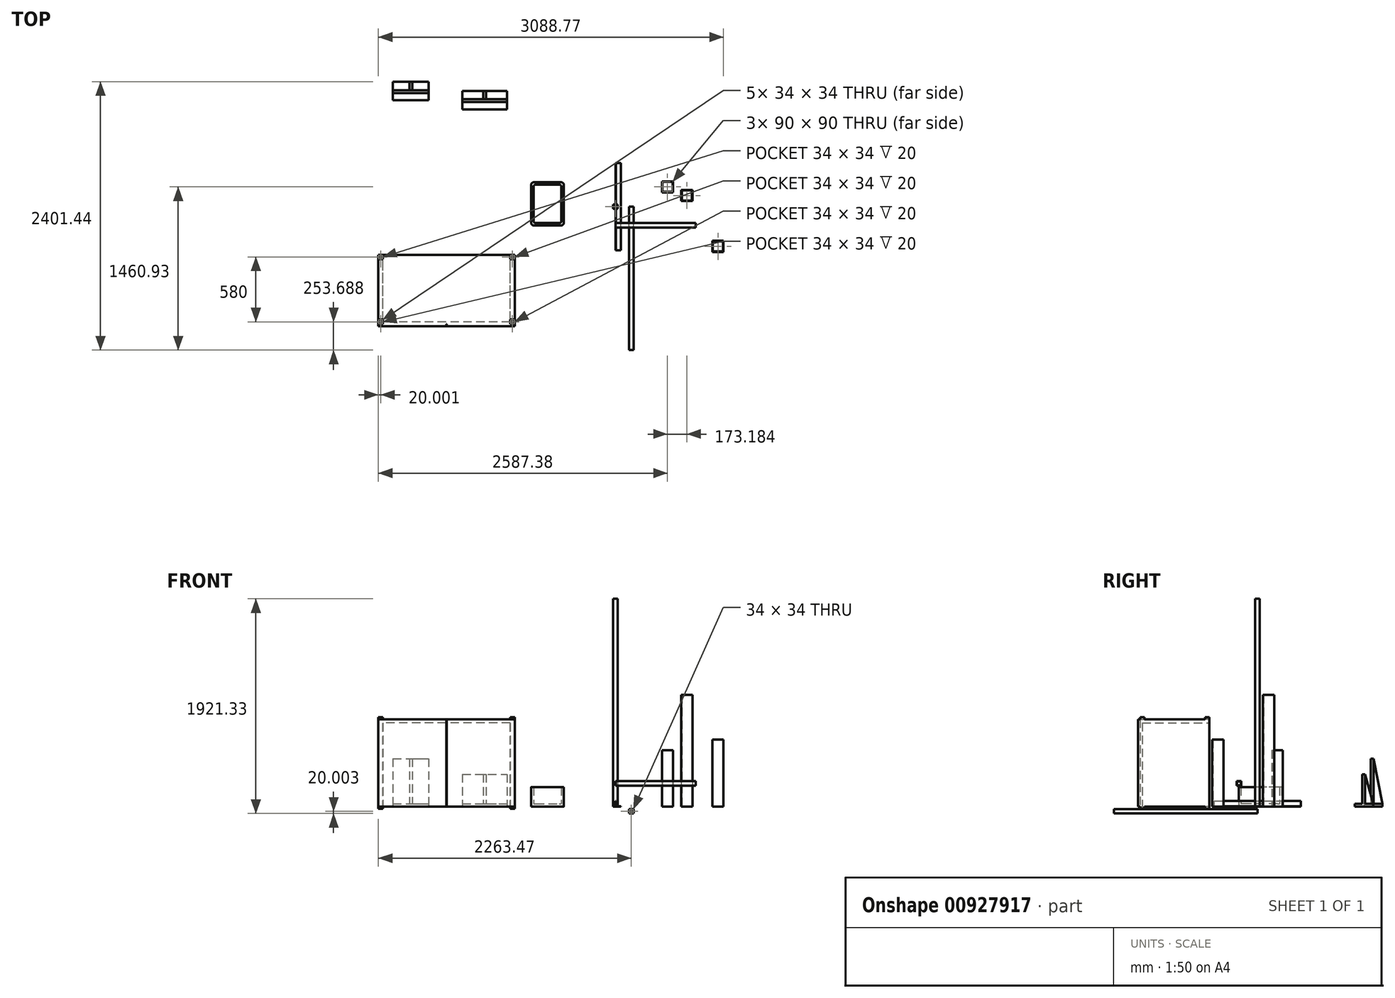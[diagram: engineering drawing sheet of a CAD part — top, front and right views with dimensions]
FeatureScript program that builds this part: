
annotation { "Feature Type Name" : "Feature", "Feature Type Description" : "" }
export const myFeature = defineFeature(function(context is Context, id is Id, definition is map)
    precondition{}
    {
        {
            var Q0;
            Q0=qCreatedBy(makeId("Front.planeOp"),FACE);
            var sketch = newSketch(context, id + "F0", { "sketchPlane" : qUnion([Q0])});
            skLineSegment(sketch, "E0", {"start": v(0, 0) * mm, "end": v(50, 0) * mm});
            skLineSegment(sketch, "E1", {"start": v(0, 0) * mm, "end": v(0, 50) * mm});
            skLineSegment(sketch, "E2", {"start": v(50, 3) * mm, "end": v(3, 3) * mm});
            skLineSegment(sketch, "E3", {"start": v(3, 50) * mm, "end": v(3, 3) * mm});
            skLineSegment(sketch, "E4", {"start": v(0, 50) * mm, "end": v(3, 50) * mm});
            skLineSegment(sketch, "E5", {"start": v(50, 0) * mm, "end": v(50, 3) * mm});
            skSolve(sketch);
        }
        {
            var Q0;
            Q0=makeQuery(id+"F0.imprint","IMPRINT",FACE,{"disambiguationData":[TD([[makeQuery(id+"F0.imprint","IMPRINT",EDGE,{"derivedFrom":sQuery(id+"F0.wireOp",EDGE,"E0")}),1.0]])]});
            extrude(context, id + "F1", {"entities" : qUnion([Q0]), "depth" : 780 * mm, "offsetDistance" : 25 * mm, "symmetric" : true});
        }
        {
            var Q0;
            Q0=qCreatedBy(makeId("Top.planeOp"),FACE);
            var sketch = newSketch(context, id + "F2", { "sketchPlane" : qUnion([Q0])});
            skLineSegment(sketch, "E6.bottom", {"start": v(-20, 20) * mm, "end": v(20, 20) * mm});
            skLineSegment(sketch, "E6.top", {"start": v(-20, -20) * mm, "end": v(20, -20) * mm});
            skLineSegment(sketch, "E6.left", {"start": v(-20, 20) * mm, "end": v(-20, -20) * mm});
            skLineSegment(sketch, "E6.right", {"start": v(20, 20) * mm, "end": v(20, -20) * mm});
            skLineSegment(sketch, "E7.0", {"start": v(-17, 17) * mm, "end": v(17, 17) * mm});
            skLineSegment(sketch, "E7.1", {"start": v(-17, 17) * mm, "end": v(-17, -17) * mm});
            skLineSegment(sketch, "E7.2", {"start": v(-17, -17) * mm, "end": v(17, -17) * mm});
            skLineSegment(sketch, "E7.3", {"start": v(17, 17) * mm, "end": v(17, -17) * mm});
            skSolve(sketch);
        }
        {
            var Q0;
            Q0=makeQuery(id+"F2.imprint","IMPRINT",FACE,{"disambiguationData":[TD([[makeQuery(id+"F2.imprint","IMPRINT",EDGE,{"derivedFrom":sQuery(id+"F2.wireOp",EDGE,"E6.bottom")}),-1.0]])]});
            extrude(context, id + "F3", {"entities" : qUnion([Q0]), "depth" : 1860 * mm, "offsetDistance" : 25 * mm});
        }
        {
            var Q0;
            Q0=qCreatedBy(makeId("Right.planeOp"),FACE);
            var sketch = newSketch(context, id + "F4", { "sketchPlane" : qUnion([Q0])});
            skLineSegment(sketch, "E8.bottom", {"start": v(-185.92, 227.9) * mm, "end": v(-145.92, 227.9) * mm});
            skLineSegment(sketch, "E8.top", {"start": v(-185.92, 187.9) * mm, "end": v(-145.92, 187.9) * mm});
            skLineSegment(sketch, "E8.left", {"start": v(-185.92, 227.9) * mm, "end": v(-185.92, 187.9) * mm});
            skLineSegment(sketch, "E8.right", {"start": v(-145.92, 227.9) * mm, "end": v(-145.92, 187.9) * mm});
            skLineSegment(sketch, "E9.0", {"start": v(-182.92, 224.9) * mm, "end": v(-148.92, 224.9) * mm});
            skLineSegment(sketch, "E9.1", {"start": v(-182.92, 224.9) * mm, "end": v(-182.92, 190.9) * mm});
            skLineSegment(sketch, "E9.2", {"start": v(-182.92, 190.9) * mm, "end": v(-148.92, 190.9) * mm});
            skLineSegment(sketch, "E9.3", {"start": v(-148.92, 224.9) * mm, "end": v(-148.92, 190.9) * mm});
            skSolve(sketch);
        }
        {
            var Q0;
            Q0 = qSketchRegion(id + "F4", true);
            extrude(context, id + "F5", {"entities" : qUnion([Q0]), "depth" : 720 * mm, "offsetDistance" : 25 * mm});
        }
        {
            var Q0;
            Q0=qCreatedBy(makeId("Front.planeOp"),FACE);
            var sketch = newSketch(context, id + "F6", { "sketchPlane" : qUnion([Q0])});
            skLineSegment(sketch, "E10.bottom", {"start": v(161.84, -21.33) * mm, "end": v(121.84, -21.33) * mm});
            skLineSegment(sketch, "E10.top", {"start": v(161.84, -61.33) * mm, "end": v(121.84, -61.33) * mm});
            skLineSegment(sketch, "E10.left", {"start": v(161.84, -21.33) * mm, "end": v(161.84, -61.33) * mm});
            skLineSegment(sketch, "E10.right", {"start": v(121.84, -21.33) * mm, "end": v(121.84, -61.33) * mm});
            skLineSegment(sketch, "E11.0", {"start": v(158.84, -24.33) * mm, "end": v(124.84, -24.33) * mm});
            skLineSegment(sketch, "E11.1", {"start": v(158.84, -24.33) * mm, "end": v(158.84, -58.33) * mm});
            skLineSegment(sketch, "E11.2", {"start": v(158.84, -58.33) * mm, "end": v(124.84, -58.33) * mm});
            skLineSegment(sketch, "E11.3", {"start": v(124.84, -24.33) * mm, "end": v(124.84, -58.33) * mm});
            skSolve(sketch);
        }
        {
            var Q0;
            Q0=makeQuery(id+"F6.imprint","IMPRINT",FACE,{"disambiguationData":[TD([[makeQuery(id+"F6.imprint","IMPRINT",EDGE,{"derivedFrom":sQuery(id+"F6.wireOp",EDGE,"E10.bottom")}),1.0]])]});
            extrude(context, id + "F7", {"entities" : qUnion([Q0]), "depth" : 1284 * mm, "offsetDistance" : 25 * mm});
        }
        {
            var Q0;
            Q0=qCreatedBy(makeId("Top.planeOp"),FACE);
            var sketch = newSketch(context, id + "F8", { "sketchPlane" : qUnion([Q0])});
            skLineSegment(sketch, "E12.bottom", {"start": v(-753.27, 217.7) * mm, "end": v(-463.27, 217.7) * mm});
            skLineSegment(sketch, "E12.top", {"start": v(-753.27, -167.3) * mm, "end": v(-463.27, -167.3) * mm});
            skLineSegment(sketch, "E12.left", {"start": v(-753.27, 217.7) * mm, "end": v(-753.27, -167.3) * mm});
            skLineSegment(sketch, "E12.right", {"start": v(-463.27, 217.7) * mm, "end": v(-463.27, -167.3) * mm});
            skSolve(sketch);
        }
        {
            var Q0;
            Q0=makeQuery(id+"F8.imprint","IMPRINT",FACE,{"disambiguationData":[TD([[makeQuery(id+"F8.imprint","IMPRINT",EDGE,{"derivedFrom":sQuery(id+"F8.wireOp",EDGE,"E12.bottom")}),-1.0]])]});
            extrude(context, id + "F9", {"entities" : qUnion([Q0]), "depth" : 25 * mm, "offsetDistance" : 25 * mm});
        }
        {
            var Q0;
            Q0=makeQuery(id+"F9.opExtrude","CAP_FACE",FACE,{"disambiguationData":[OSD([sQuery(id+"F8.wireOp",EDGE,"E12.bottom"),sQuery(id+"F8.wireOp",EDGE,"E12.top"),sQuery(id+"F8.wireOp",EDGE,"E12.left"),sQuery(id+"F8.wireOp",EDGE,"E12.right")])],"isStart":false});
            var sketch = newSketch(context, id + "F10", { "sketchPlane" : qUnion([Q0])});
            skLineSegment(sketch, "E13.0", {"start": v(-733.27, 197.7) * mm, "end": v(-483.27, 197.7) * mm});
            skLineSegment(sketch, "E13.1", {"start": v(-733.27, 197.7) * mm, "end": v(-733.27, -147.3) * mm});
            skLineSegment(sketch, "E13.2", {"start": v(-733.27, -147.3) * mm, "end": v(-483.27, -147.3) * mm});
            skLineSegment(sketch, "E13.3", {"start": v(-483.27, 197.7) * mm, "end": v(-483.27, -147.3) * mm});
            skSolve(sketch);
        }
        {
            var Q0;
            Q0=makeQuery(id+"F10.imprint","IMPRINT",FACE,{"disambiguationData":[TD([[makeQuery(id+"F10.imprint","IMPRINT",EDGE,{"derivedFrom":sQuery(id+"F10.wireOp",EDGE,"E13.0")}),1.0]])]});
            extrude(context, id + "F11", {"entities" : qUnion([Q0]), "operationType" : NewBodyOperationType.ADD, "depth" : 150 * mm, "offsetDistance" : 25 * mm});
        }
        {
            var Q0;
            {var subQ0=sQuery(id+"F8.wireOp",EDGE,"E12.right");var subQ1=sQuery(id+"F8.wireOp",EDGE,"E12.top");Q0=makeQuery(id+"F11.boolean.opBoolean","MERGE",EDGE,{"derivedFrom":[makeQuery(id+"F9.opExtrude","SWEPT_EDGE",EDGE,{"disambiguationData":[OSD([subQ1,subQ0])]}),makeQuery(id+"F11.opExtrude","SWEPT_EDGE",EDGE,{"disambiguationData":[OSD([subQ1,subQ0])]})]});}
            var Q1;
            {var subQ0=sQuery(id+"F8.wireOp",EDGE,"E12.right");var subQ1=sQuery(id+"F8.wireOp",EDGE,"E12.bottom");Q1=makeQuery(id+"F11.boolean.opBoolean","MERGE",EDGE,{"derivedFrom":[makeQuery(id+"F9.opExtrude","SWEPT_EDGE",EDGE,{"disambiguationData":[OSD([subQ1,subQ0])]}),makeQuery(id+"F11.opExtrude","SWEPT_EDGE",EDGE,{"disambiguationData":[OSD([subQ1,subQ0])]})]});}
            var Q2;
            {var subQ0=sQuery(id+"F8.wireOp",EDGE,"E12.left");var subQ1=sQuery(id+"F8.wireOp",EDGE,"E12.top");Q2=makeQuery(id+"F11.boolean.opBoolean","MERGE",EDGE,{"derivedFrom":[makeQuery(id+"F9.opExtrude","SWEPT_EDGE",EDGE,{"disambiguationData":[OSD([subQ1,subQ0])]}),makeQuery(id+"F11.opExtrude","SWEPT_EDGE",EDGE,{"disambiguationData":[OSD([subQ1,subQ0])]})]});}
            var Q3;
            {var subQ0=sQuery(id+"F8.wireOp",EDGE,"E12.left");var subQ1=sQuery(id+"F8.wireOp",EDGE,"E12.bottom");Q3=makeQuery(id+"F11.boolean.opBoolean","MERGE",EDGE,{"derivedFrom":[makeQuery(id+"F9.opExtrude","SWEPT_EDGE",EDGE,{"disambiguationData":[OSD([subQ1,subQ0])]}),makeQuery(id+"F11.opExtrude","SWEPT_EDGE",EDGE,{"disambiguationData":[OSD([subQ1,subQ0])]})]});}
            var Q4;
            Q4=makeQuery(id+"F11.opExtrude","SWEPT_EDGE",EDGE,{"disambiguationData":[OSD([sQuery(id+"F10.wireOp",EDGE,"E13.0"),sQuery(id+"F10.wireOp",EDGE,"E13.1")])]});
            var Q5;
            Q5=makeQuery(id+"F11.opExtrude","SWEPT_EDGE",EDGE,{"disambiguationData":[OSD([sQuery(id+"F10.wireOp",EDGE,"E13.0"),sQuery(id+"F10.wireOp",EDGE,"E13.3")])]});
            var Q6;
            Q6=makeQuery(id+"F11.opExtrude","SWEPT_EDGE",EDGE,{"disambiguationData":[OSD([sQuery(id+"F10.wireOp",EDGE,"E13.2"),sQuery(id+"F10.wireOp",EDGE,"E13.3")])]});
            var Q7;
            Q7=makeQuery(id+"F11.opExtrude","SWEPT_EDGE",EDGE,{"disambiguationData":[OSD([sQuery(id+"F10.wireOp",EDGE,"E13.1"),sQuery(id+"F10.wireOp",EDGE,"E13.2")])]});
            fillet(context, id + "F12", {"entities" : qUnion([Q0, Q1, Q2, Q3, Q4, Q5, Q6, Q7]), "radius" : 20 * mm, "tangentPropagation" : true, "allowEdgeOverflow" : false});
        }
        {
            var Q0;
            Q0=qCreatedBy(makeId("Top.planeOp"),FACE);
            var sketch = newSketch(context, id + "F13", { "sketchPlane" : qUnion([Q0])});
            skLineSegment(sketch, "E14.bottom", {"start": v(415.75, 126.93) * mm, "end": v(515.75, 126.93) * mm});
            skLineSegment(sketch, "E14.top", {"start": v(415.75, 226.93) * mm, "end": v(515.75, 226.93) * mm});
            skLineSegment(sketch, "E14.left", {"start": v(415.75, 126.93) * mm, "end": v(415.75, 226.93) * mm});
            skLineSegment(sketch, "E14.right", {"start": v(515.75, 126.93) * mm, "end": v(515.75, 226.93) * mm});
            skLineSegment(sketch, "E15.0", {"start": v(420.75, 131.93) * mm, "end": v(510.75, 131.93) * mm});
            skLineSegment(sketch, "E15.1", {"start": v(420.75, 131.93) * mm, "end": v(420.75, 221.93) * mm});
            skLineSegment(sketch, "E15.2", {"start": v(420.75, 221.93) * mm, "end": v(510.75, 221.93) * mm});
            skLineSegment(sketch, "E15.3", {"start": v(510.75, 131.93) * mm, "end": v(510.75, 221.93) * mm});
            skSolve(sketch);
        }
        {
            var Q0;
            Q0 = qSketchRegion(id + "F13", true);
            extrude(context, id + "F14", {"entities" : qUnion([Q0]), "depth" : 505 * mm, "offsetDistance" : 25 * mm});
        }
        {
            var Q0;
            Q0=qCreatedBy(makeId("Top.planeOp"),FACE);
            var sketch = newSketch(context, id + "F15", { "sketchPlane" : qUnion([Q0])});
            skLineSegment(sketch, "E16.bottom", {"start": v(867.14, -305.03) * mm, "end": v(967.14, -305.03) * mm});
            skLineSegment(sketch, "E16.top", {"start": v(867.14, -405.03) * mm, "end": v(967.14, -405.03) * mm});
            skLineSegment(sketch, "E16.left", {"start": v(867.14, -305.03) * mm, "end": v(867.14, -405.03) * mm});
            skLineSegment(sketch, "E16.right", {"start": v(967.14, -305.03) * mm, "end": v(967.14, -405.03) * mm});
            skLineSegment(sketch, "E17.0", {"start": v(872.14, -310.03) * mm, "end": v(962.14, -310.03) * mm});
            skLineSegment(sketch, "E17.1", {"start": v(872.14, -310.03) * mm, "end": v(872.14, -400.03) * mm});
            skLineSegment(sketch, "E17.2", {"start": v(872.14, -400.03) * mm, "end": v(962.14, -400.03) * mm});
            skLineSegment(sketch, "E17.3", {"start": v(962.14, -310.03) * mm, "end": v(962.14, -400.03) * mm});
            skSolve(sketch);
        }
        {
            var Q0;
            Q0 = qSketchRegion(id + "F15", true);
            extrude(context, id + "F16", {"entities" : qUnion([Q0]), "depth" : 600 * mm, "offsetDistance" : 25 * mm});
        }
        {
            var Q0;
            Q0=qCreatedBy(makeId("Top.planeOp"),FACE);
            var sketch = newSketch(context, id + "F17", { "sketchPlane" : qUnion([Q0])});
            skLineSegment(sketch, "E18.bottom", {"start": v(588.94, 50.04) * mm, "end": v(688.94, 50.04) * mm});
            skLineSegment(sketch, "E18.top", {"start": v(588.94, 150.04) * mm, "end": v(688.94, 150.04) * mm});
            skLineSegment(sketch, "E18.left", {"start": v(588.94, 50.04) * mm, "end": v(588.94, 150.04) * mm});
            skLineSegment(sketch, "E18.right", {"start": v(688.94, 50.04) * mm, "end": v(688.94, 150.04) * mm});
            skLineSegment(sketch, "E19.0", {"start": v(683.94, 55.04) * mm, "end": v(683.94, 145.04) * mm});
            skLineSegment(sketch, "E19.1", {"start": v(593.94, 55.04) * mm, "end": v(683.94, 55.04) * mm});
            skLineSegment(sketch, "E19.2", {"start": v(593.94, 55.04) * mm, "end": v(593.94, 145.04) * mm});
            skLineSegment(sketch, "E19.3", {"start": v(593.94, 145.04) * mm, "end": v(683.94, 145.04) * mm});
            skSolve(sketch);
        }
        {
            var Q0;
            Q0 = qSketchRegion(id + "F17", true);
            extrude(context, id + "F18", {"entities" : qUnion([Q0]), "depth" : 1000 * mm, "offsetDistance" : 25 * mm});
        }
        {
            var Q0;
            Q0=qCreatedBy(makeId("Top.planeOp"),FACE);
            var sketch = newSketch(context, id + "F19", { "sketchPlane" : qUnion([Q0])});
            skLineSegment(sketch, "E20.bottom", {"start": v(-901.63, -430.31) * mm, "end": v(-2121.63, -430.31) * mm});
            skLineSegment(sketch, "E20.top", {"start": v(-901.63, -1050.31) * mm, "end": v(-2121.63, -1050.31) * mm});
            skLineSegment(sketch, "E20.left", {"start": v(-901.63, -430.31) * mm, "end": v(-901.63, -1050.31) * mm});
            skLineSegment(sketch, "E20.right", {"start": v(-2121.63, -430.31) * mm, "end": v(-2121.63, -1050.31) * mm});
            skSolve(sketch);
        }
        {
            var Q0;
            Q0=makeQuery(id+"F19.imprint","IMPRINT",FACE,{"disambiguationData":[TD([[makeQuery(id+"F19.imprint","IMPRINT",EDGE,{"derivedFrom":sQuery(id+"F19.wireOp",EDGE,"E20.bottom")}),1.0]])]});
            extrude(context, id + "F20", {"entities" : qUnion([Q0]), "depth" : 780 * mm, "offsetDistance" : 25 * mm});
        }
        {
            var Q0;
            Q0=makeQuery(id+"F20.opExtrude","CAP_FACE",FACE,{"disambiguationData":[OSD([sQuery(id+"F19.wireOp",EDGE,"E20.bottom"),sQuery(id+"F19.wireOp",EDGE,"E20.top"),sQuery(id+"F19.wireOp",EDGE,"E20.left"),sQuery(id+"F19.wireOp",EDGE,"E20.right")])],"isStart":false});
            var sketch = newSketch(context, id + "F21", { "sketchPlane" : qUnion([Q0])});
            skLineSegment(sketch, "E21.bottom", {"start": v(-2121.63, -430.31) * mm, "end": v(-2081.63, -430.31) * mm});
            skLineSegment(sketch, "E21.top", {"start": v(-2121.63, -470.31) * mm, "end": v(-2081.63, -470.31) * mm});
            skLineSegment(sketch, "E21.left", {"start": v(-2121.63, -430.31) * mm, "end": v(-2121.63, -470.31) * mm});
            skLineSegment(sketch, "E21.right", {"start": v(-2081.63, -430.31) * mm, "end": v(-2081.63, -470.31) * mm});
            skLineSegment(sketch, "E22.0", {"start": v(-2118.63, -433.31) * mm, "end": v(-2084.63, -433.31) * mm});
            skLineSegment(sketch, "E22.1", {"start": v(-2118.63, -433.31) * mm, "end": v(-2118.63, -467.31) * mm});
            skLineSegment(sketch, "E22.2", {"start": v(-2118.63, -467.31) * mm, "end": v(-2084.63, -467.31) * mm});
            skLineSegment(sketch, "E22.3", {"start": v(-2084.63, -433.31) * mm, "end": v(-2084.63, -467.31) * mm});
            skLineSegment(sketch, "E23.bottom", {"start": v(-901.63, -430.31) * mm, "end": v(-941.63, -430.31) * mm});
            skLineSegment(sketch, "E23.top", {"start": v(-901.63, -470.31) * mm, "end": v(-941.63, -470.31) * mm});
            skLineSegment(sketch, "E23.left", {"start": v(-901.63, -430.31) * mm, "end": v(-901.63, -470.31) * mm});
            skLineSegment(sketch, "E23.right", {"start": v(-941.63, -430.31) * mm, "end": v(-941.63, -470.31) * mm});
            skLineSegment(sketch, "E24.0", {"start": v(-904.63, -433.31) * mm, "end": v(-938.63, -433.31) * mm});
            skLineSegment(sketch, "E24.1", {"start": v(-904.63, -433.31) * mm, "end": v(-904.63, -467.31) * mm});
            skLineSegment(sketch, "E24.2", {"start": v(-904.63, -467.31) * mm, "end": v(-938.63, -467.31) * mm});
            skLineSegment(sketch, "E24.3", {"start": v(-938.63, -433.31) * mm, "end": v(-938.63, -467.31) * mm});
            skLineSegment(sketch, "E25.bottom", {"start": v(-901.63, -1050.31) * mm, "end": v(-941.63, -1050.31) * mm});
            skLineSegment(sketch, "E25.top", {"start": v(-901.63, -1010.31) * mm, "end": v(-941.63, -1010.31) * mm});
            skLineSegment(sketch, "E25.left", {"start": v(-901.63, -1050.31) * mm, "end": v(-901.63, -1010.31) * mm});
            skLineSegment(sketch, "E25.right", {"start": v(-941.63, -1050.31) * mm, "end": v(-941.63, -1010.31) * mm});
            skLineSegment(sketch, "E26.bottom", {"start": v(-2121.63, -1050.31) * mm, "end": v(-2081.63, -1050.31) * mm});
            skLineSegment(sketch, "E26.top", {"start": v(-2121.63, -1010.31) * mm, "end": v(-2081.63, -1010.31) * mm});
            skLineSegment(sketch, "E26.left", {"start": v(-2121.63, -1050.31) * mm, "end": v(-2121.63, -1010.31) * mm});
            skLineSegment(sketch, "E26.right", {"start": v(-2081.63, -1050.31) * mm, "end": v(-2081.63, -1010.31) * mm});
            skLineSegment(sketch, "E27.0", {"start": v(-2118.63, -1013.31) * mm, "end": v(-2084.63, -1013.31) * mm});
            skLineSegment(sketch, "E27.1", {"start": v(-2118.63, -1047.31) * mm, "end": v(-2118.63, -1013.31) * mm});
            skLineSegment(sketch, "E27.2", {"start": v(-2118.63, -1047.31) * mm, "end": v(-2084.63, -1047.31) * mm});
            skLineSegment(sketch, "E27.3", {"start": v(-2084.63, -1047.31) * mm, "end": v(-2084.63, -1013.31) * mm});
            skLineSegment(sketch, "E28.0", {"start": v(-904.63, -1013.31) * mm, "end": v(-938.63, -1013.31) * mm});
            skLineSegment(sketch, "E28.1", {"start": v(-904.63, -1047.31) * mm, "end": v(-904.63, -1013.31) * mm});
            skLineSegment(sketch, "E28.2", {"start": v(-904.63, -1047.31) * mm, "end": v(-938.63, -1047.31) * mm});
            skLineSegment(sketch, "E28.3", {"start": v(-938.63, -1047.31) * mm, "end": v(-938.63, -1013.31) * mm});
            skSolve(sketch);
        }
        {
            var Q0;
            Q0 = qSketchRegion(id + "F21", true);
            extrude(context, id + "F22", {"entities" : qUnion([Q0]), "operationType" : NewBodyOperationType.ADD, "depth" : 20 * mm, "offsetDistance" : 25 * mm});
        }
        {
            var Q0;
            Q0=makeQuery(id+"F22.boolean.opBoolean","MERGE",FACE,{"derivedFrom":[makeQuery(id+"F20.opExtrude","SWEPT_FACE",FACE,{"disambiguationData":[OSD([sQuery(id+"F19.wireOp",EDGE,"E20.top")])]}),makeQuery(id+"F22.opExtrude","SWEPT_FACE",FACE,{"disambiguationData":[OSD([sQuery(id+"F21.wireOp",EDGE,"E25.bottom")])]}),makeQuery(id+"F22.opExtrude","SWEPT_FACE",FACE,{"disambiguationData":[OSD([sQuery(id+"F21.wireOp",EDGE,"E26.bottom")])]})]});
            var sketch = newSketch(context, id + "F23", { "sketchPlane" : qUnion([Q0])});
            skLineSegment(sketch, "E29", {"start": v(-1511.63, 780) * mm, "end": v(-1511.63, 0) * mm, "construction": true});
            skPoint(sketch, "E30", {"position": v(-1509.63, 780) * mm});
            skPoint(sketch, "E31", {"position": v(-1513.63, 780) * mm});
            skLineSegment(sketch, "E32.bottom", {"start": v(-1509.63, 780) * mm, "end": v(-901.63, 780) * mm});
            skLineSegment(sketch, "E32.top", {"start": v(-1509.63, 0) * mm, "end": v(-901.63, 0) * mm});
            skLineSegment(sketch, "E32.left", {"start": v(-1509.63, 780) * mm, "end": v(-1509.63, 0) * mm});
            skLineSegment(sketch, "E32.right", {"start": v(-901.63, 780) * mm, "end": v(-901.63, 0) * mm});
            skLineSegment(sketch, "E33.bottom", {"start": v(-1513.63, 780) * mm, "end": v(-2121.63, 780) * mm});
            skLineSegment(sketch, "E33.top", {"start": v(-1513.63, 0) * mm, "end": v(-2121.63, 0) * mm});
            skLineSegment(sketch, "E33.left", {"start": v(-1513.63, 780) * mm, "end": v(-1513.63, 0) * mm});
            skLineSegment(sketch, "E33.right", {"start": v(-2121.63, 780) * mm, "end": v(-2121.63, 0) * mm});
            skSolve(sketch);
        }
        {
            var Q0;
            Q0=makeQuery(id+"F23.imprint","IMPRINT",FACE,{"disambiguationData":[TD([[makeQuery(id+"F23.imprint","IMPRINT",EDGE,{"derivedFrom":sQuery(id+"F23.wireOp",EDGE,"E32.top")}),-1.0]])]});
            var Q1;
            Q1=makeQuery(id+"F23.imprint","IMPRINT",FACE,{"disambiguationData":[TD([[makeQuery(id+"F23.imprint","IMPRINT",EDGE,{"derivedFrom":sQuery(id+"F23.wireOp",EDGE,"E33.top")}),-1.0]])]});
            extrude(context, id + "F24", {"entities" : qUnion([Q0, Q1]), "operationType" : NewBodyOperationType.ADD, "depth" : 20 * mm, "offsetDistance" : 25 * mm});
        }
        {
            var Q0;
            Q0=makeQuery(id+"F24.boolean.opBoolean","MERGE",FACE,{"derivedFrom":[makeQuery(id+"F20.opExtrude","CAP_FACE",FACE,{"disambiguationData":[OSD([sQuery(id+"F19.wireOp",EDGE,"E20.bottom"),sQuery(id+"F19.wireOp",EDGE,"E20.top"),sQuery(id+"F19.wireOp",EDGE,"E20.left"),sQuery(id+"F19.wireOp",EDGE,"E20.right")])],"isStart":true}),makeQuery(id+"F24.opExtrude","SWEPT_FACE",FACE,{"disambiguationData":[OSD([sQuery(id+"F23.wireOp",EDGE,"E32.top")])]}),makeQuery(id+"F24.opExtrude","SWEPT_FACE",FACE,{"disambiguationData":[OSD([sQuery(id+"F23.wireOp",EDGE,"E33.top")])]})]});
            var sketch = newSketch(context, id + "F25", { "sketchPlane" : qUnion([Q0])});
            skPoint(sketch, "E34", {"position": v(-2121.63, 1050.31) * mm});
            skPoint(sketch, "E35", {"position": v(-901.63, 1050.31) * mm});
            skLineSegment(sketch, "E36.bottom", {"start": v(-901.63, 1050.31) * mm, "end": v(-941.63, 1050.31) * mm});
            skLineSegment(sketch, "E36.top", {"start": v(-901.63, 1010.31) * mm, "end": v(-941.63, 1010.31) * mm});
            skLineSegment(sketch, "E36.left", {"start": v(-901.63, 1050.31) * mm, "end": v(-901.63, 1010.31) * mm});
            skLineSegment(sketch, "E36.right", {"start": v(-941.63, 1050.31) * mm, "end": v(-941.63, 1010.31) * mm});
            skLineSegment(sketch, "E37.0", {"start": v(-904.63, 1013.31) * mm, "end": v(-938.63, 1013.31) * mm});
            skLineSegment(sketch, "E37.1", {"start": v(-904.63, 1047.31) * mm, "end": v(-904.63, 1013.31) * mm});
            skLineSegment(sketch, "E37.2", {"start": v(-904.63, 1047.31) * mm, "end": v(-938.63, 1047.31) * mm});
            skLineSegment(sketch, "E37.3", {"start": v(-938.63, 1047.31) * mm, "end": v(-938.63, 1013.31) * mm});
            skLineSegment(sketch, "E38.bottom", {"start": v(-2121.63, 1050.31) * mm, "end": v(-2081.63, 1050.31) * mm});
            skLineSegment(sketch, "E38.top", {"start": v(-2121.63, 1010.31) * mm, "end": v(-2081.63, 1010.31) * mm});
            skLineSegment(sketch, "E38.left", {"start": v(-2121.63, 1050.31) * mm, "end": v(-2121.63, 1010.31) * mm});
            skLineSegment(sketch, "E38.right", {"start": v(-2081.63, 1050.31) * mm, "end": v(-2081.63, 1010.31) * mm});
            skLineSegment(sketch, "E39.0", {"start": v(-2118.63, 1013.31) * mm, "end": v(-2084.63, 1013.31) * mm});
            skLineSegment(sketch, "E39.1", {"start": v(-2118.63, 1047.31) * mm, "end": v(-2118.63, 1013.31) * mm});
            skLineSegment(sketch, "E39.2", {"start": v(-2118.63, 1047.31) * mm, "end": v(-2084.63, 1047.31) * mm});
            skLineSegment(sketch, "E39.3", {"start": v(-2084.63, 1047.31) * mm, "end": v(-2084.63, 1013.31) * mm});
            skLineSegment(sketch, "E40.bottom", {"start": v(-2121.63, 430.31) * mm, "end": v(-2081.63, 430.31) * mm});
            skLineSegment(sketch, "E40.top", {"start": v(-2121.63, 470.31) * mm, "end": v(-2081.63, 470.31) * mm});
            skLineSegment(sketch, "E40.left", {"start": v(-2121.63, 430.31) * mm, "end": v(-2121.63, 470.31) * mm});
            skLineSegment(sketch, "E40.right", {"start": v(-2081.63, 430.31) * mm, "end": v(-2081.63, 470.31) * mm});
            skLineSegment(sketch, "E41.0", {"start": v(-2084.63, 433.31) * mm, "end": v(-2084.63, 467.31) * mm});
            skLineSegment(sketch, "E41.1", {"start": v(-2118.63, 433.31) * mm, "end": v(-2084.63, 433.31) * mm});
            skLineSegment(sketch, "E41.2", {"start": v(-2118.63, 433.31) * mm, "end": v(-2118.63, 467.31) * mm});
            skLineSegment(sketch, "E41.3", {"start": v(-2118.63, 467.31) * mm, "end": v(-2084.63, 467.31) * mm});
            skLineSegment(sketch, "E42.bottom", {"start": v(-901.63, 430.31) * mm, "end": v(-941.63, 430.31) * mm});
            skLineSegment(sketch, "E42.top", {"start": v(-901.63, 470.31) * mm, "end": v(-941.63, 470.31) * mm});
            skLineSegment(sketch, "E42.left", {"start": v(-901.63, 430.31) * mm, "end": v(-901.63, 470.31) * mm});
            skLineSegment(sketch, "E42.right", {"start": v(-941.63, 430.31) * mm, "end": v(-941.63, 470.31) * mm});
            skLineSegment(sketch, "E43.0", {"start": v(-904.63, 467.31) * mm, "end": v(-938.63, 467.31) * mm});
            skLineSegment(sketch, "E43.1", {"start": v(-904.63, 433.31) * mm, "end": v(-904.63, 467.31) * mm});
            skLineSegment(sketch, "E43.2", {"start": v(-904.63, 433.31) * mm, "end": v(-938.63, 433.31) * mm});
            skLineSegment(sketch, "E43.3", {"start": v(-938.63, 433.31) * mm, "end": v(-938.63, 467.31) * mm});
            skSolve(sketch);
        }
        {
            var Q0;
            Q0 = qSketchRegion(id + "F25", true);
            extrude(context, id + "F26", {"entities" : qUnion([Q0]), "operationType" : NewBodyOperationType.ADD, "depth" : 20 * mm, "offsetDistance" : 25 * mm});
        }
        {
            var Q0;
            Q0=qCreatedBy(makeId("Top.planeOp"),FACE);
            var sketch = newSketch(context, id + "F27", { "sketchPlane" : qUnion([Q0])});
            skLineSegment(sketch, "E44.bottom", {"start": v(-1991.3, 1117.44) * mm, "end": v(-1671.3, 1117.44) * mm});
            skLineSegment(sketch, "E44.top", {"start": v(-1991.3, 952.44) * mm, "end": v(-1671.3, 952.44) * mm});
            skLineSegment(sketch, "E44.left", {"start": v(-1991.3, 1117.44) * mm, "end": v(-1991.3, 952.44) * mm});
            skLineSegment(sketch, "E44.right", {"start": v(-1671.3, 1117.44) * mm, "end": v(-1671.3, 952.44) * mm});
            skSolve(sketch);
        }
        {
            var Q0;
            Q0 = qSketchRegion(id + "F27", true);
            extrude(context, id + "F28", {"entities" : qUnion([Q0]), "depth" : 25 * mm, "offsetDistance" : 25 * mm});
        }
        {
            var Q0;
            Q0=makeQuery(id+"F28.opExtrude","CAP_FACE",FACE,{"disambiguationData":[OSD([sQuery(id+"F27.wireOp",EDGE,"E44.bottom"),sQuery(id+"F27.wireOp",EDGE,"E44.top"),sQuery(id+"F27.wireOp",EDGE,"E44.left"),sQuery(id+"F27.wireOp",EDGE,"E44.right")])],"isStart":false});
            var sketch = newSketch(context, id + "F29", { "sketchPlane" : qUnion([Q0])});
            skLineSegment(sketch, "E45.bottom", {"start": v(-1991.3, 1015.12) * mm, "end": v(-1671.3, 1015.12) * mm});
            skLineSegment(sketch, "E45.top", {"start": v(-1991.3, 1040.12) * mm, "end": v(-1671.3, 1040.12) * mm});
            skLineSegment(sketch, "E45.left", {"start": v(-1991.3, 1015.12) * mm, "end": v(-1991.3, 1040.12) * mm});
            skLineSegment(sketch, "E45.right", {"start": v(-1671.3, 1015.12) * mm, "end": v(-1671.3, 1040.12) * mm});
            skSolve(sketch);
        }
        {
            var Q0;
            Q0 = qSketchRegion(id + "F29", true);
            extrude(context, id + "F30", {"entities" : qUnion([Q0]), "operationType" : NewBodyOperationType.ADD, "depth" : (430 - 25) * mm, "offsetDistance" : 25 * mm});
        }
        {
            var Q0;
            {var subQ0=sQuery(id+"F27.wireOp",EDGE,"E44.left");var subQ1=sQuery(id+"F27.wireOp",EDGE,"E44.right");var subQ2=sQuery(id+"F27.wireOp",EDGE,"E44.bottom");Q0=makeQuery(id+"F30.boolean.opBoolean","SPLIT",FACE,{"disambiguationData":[TD([makeQuery(id+"F28.opExtrude","SWEPT_FACE",FACE,{"disambiguationData":[OSD([subQ2])]})])],"derivedFrom":makeQuery(id+"F28.opExtrude","CAP_FACE",FACE,{"disambiguationData":[OSD([subQ2,sQuery(id+"F27.wireOp",EDGE,"E44.top"),subQ0,subQ1])],"isStart":false})});}
            var sketch = newSketch(context, id + "F31", { "sketchPlane" : qUnion([Q0])});
            skLineSegment(sketch, "E46.bottom", {"start": v(-1843.8, 1117.44) * mm, "end": v(-1818.8, 1117.44) * mm});
            skLineSegment(sketch, "E46.top", {"start": v(-1843.8, 1040.12) * mm, "end": v(-1818.8, 1040.12) * mm});
            skLineSegment(sketch, "E46.left", {"start": v(-1843.8, 1117.44) * mm, "end": v(-1843.8, 1040.12) * mm});
            skLineSegment(sketch, "E46.right", {"start": v(-1818.8, 1117.44) * mm, "end": v(-1818.8, 1040.12) * mm});
            skSolve(sketch);
        }
        {
            var Q0;
            Q0=makeQuery(id+"F31.imprint","IMPRINT",FACE,{"disambiguationData":[TD([[makeQuery(id+"F31.imprint","IMPRINT",EDGE,{"derivedFrom":sQuery(id+"F31.wireOp",EDGE,"E46.bottom")}),-1.0]])]});
            var Q1;
            Q1=makeQuery(id+"F28.opExtrude","SWEPT_BODY",BODY,{"disambiguationData":[OSD([sQuery(id+"F27.wireOp",EDGE,"E44.bottom"),sQuery(id+"F27.wireOp",EDGE,"E44.top"),sQuery(id+"F27.wireOp",EDGE,"E44.left"),sQuery(id+"F27.wireOp",EDGE,"E44.right")])]});
            extrude(context, id + "F32", {"entities" : qUnion([Q0]), "operationType" : NewBodyOperationType.ADD, "depth" : 405 * mm, "endBoundEntityBody" : qUnion([Q1]), "offsetDistance" : 25 * mm});
        }
        {
            var Q0;
            Q0=makeQuery(id+"F32.opExtrude","SWEPT_FACE",FACE,{"disambiguationData":[OSD([sQuery(id+"F31.wireOp",EDGE,"E46.right")])]});
            var sketch = newSketch(context, id + "F33", { "sketchPlane" : qUnion([Q0])});
            skLineSegment(sketch, "E47", {"start": v(1040.12, 430) * mm, "end": v(1117.44, 25) * mm});
            skLineSegment(sketch, "E48", {"start": v(1117.44, 25) * mm, "end": v(1117.44, 430) * mm});
            skLineSegment(sketch, "E49", {"start": v(1117.44, 430) * mm, "end": v(1040.12, 430) * mm});
            skSolve(sketch);
        }
        {
            var Q0;
            Q0=makeQuery(id+"F33.imprint","IMPRINT",FACE,{"disambiguationData":[TD([[makeQuery(id+"F33.imprint","IMPRINT",EDGE,{"derivedFrom":sQuery(id+"F33.wireOp",EDGE,"E47")}),1.0]])]});
            extrude(context, id + "F34", {"entities" : qUnion([Q0]), "operationType" : NewBodyOperationType.REMOVE, "oppositeDirection" : true, "depth" : 25 * mm, "offsetDistance" : 25 * mm});
        }
        {
            var Q0;
            Q0=qCreatedBy(makeId("Top.planeOp"),FACE);
            var sketch = newSketch(context, id + "F35", { "sketchPlane" : qUnion([Q0])});
            skLineSegment(sketch, "E50.bottom", {"start": v(-1370.16, 1036.17) * mm, "end": v(-970.16, 1036.17) * mm});
            skLineSegment(sketch, "E50.top", {"start": v(-1370.16, 871.17) * mm, "end": v(-970.16, 871.17) * mm});
            skLineSegment(sketch, "E50.left", {"start": v(-1370.16, 1036.17) * mm, "end": v(-1370.16, 871.17) * mm});
            skLineSegment(sketch, "E50.right", {"start": v(-970.16, 1036.17) * mm, "end": v(-970.16, 871.17) * mm});
            skSolve(sketch);
        }
        {
            var Q0;
            Q0 = qSketchRegion(id + "F35", true);
            extrude(context, id + "F36", {"entities" : qUnion([Q0]), "depth" : 25 * mm, "offsetDistance" : 25 * mm});
        }
        {
            var Q0;
            Q0=makeQuery(id+"F36.opExtrude","CAP_FACE",FACE,{"disambiguationData":[OSD([sQuery(id+"F35.wireOp",EDGE,"E50.bottom"),sQuery(id+"F35.wireOp",EDGE,"E50.top"),sQuery(id+"F35.wireOp",EDGE,"E50.left"),sQuery(id+"F35.wireOp",EDGE,"E50.right")])],"isStart":false});
            var sketch = newSketch(context, id + "F37", { "sketchPlane" : qUnion([Q0])});
            skLineSegment(sketch, "E51.bottom", {"start": v(-1370.16, 937.28) * mm, "end": v(-970.16, 937.28) * mm});
            skLineSegment(sketch, "E51.top", {"start": v(-1370.16, 962.28) * mm, "end": v(-970.16, 962.28) * mm});
            skLineSegment(sketch, "E51.left", {"start": v(-1370.16, 937.28) * mm, "end": v(-1370.16, 962.28) * mm});
            skLineSegment(sketch, "E51.right", {"start": v(-970.16, 937.28) * mm, "end": v(-970.16, 962.28) * mm});
            skSolve(sketch);
        }
        {
            var Q0;
            Q0 = qSketchRegion(id + "F37", true);
            extrude(context, id + "F38", {"entities" : qUnion([Q0]), "operationType" : NewBodyOperationType.ADD, "depth" : (290 - 25) * mm, "offsetDistance" : 25 * mm});
        }
        {
            var Q0;
            {var subQ0=sQuery(id+"F35.wireOp",EDGE,"E50.left");var subQ1=sQuery(id+"F35.wireOp",EDGE,"E50.right");var subQ2=sQuery(id+"F35.wireOp",EDGE,"E50.bottom");Q0=makeQuery(id+"F38.boolean.opBoolean","SPLIT",FACE,{"disambiguationData":[TD([makeQuery(id+"F36.opExtrude","SWEPT_FACE",FACE,{"disambiguationData":[OSD([subQ2])]})])],"derivedFrom":makeQuery(id+"F36.opExtrude","CAP_FACE",FACE,{"disambiguationData":[OSD([subQ2,sQuery(id+"F35.wireOp",EDGE,"E50.top"),subQ0,subQ1])],"isStart":false})});}
            var sketch = newSketch(context, id + "F39", { "sketchPlane" : qUnion([Q0])});
            skLineSegment(sketch, "E52.bottom", {"start": v(-1182.66, 1036.17) * mm, "end": v(-1157.66, 1036.17) * mm});
            skLineSegment(sketch, "E52.top", {"start": v(-1182.66, 962.28) * mm, "end": v(-1157.66, 962.28) * mm});
            skLineSegment(sketch, "E52.left", {"start": v(-1182.66, 1036.17) * mm, "end": v(-1182.66, 962.28) * mm});
            skLineSegment(sketch, "E52.right", {"start": v(-1157.66, 1036.17) * mm, "end": v(-1157.66, 962.28) * mm});
            skSolve(sketch);
        }
        {
            var Q0;
            Q0 = qSketchRegion(id + "F39", true);
            extrude(context, id + "F40", {"entities" : qUnion([Q0]), "operationType" : NewBodyOperationType.ADD, "depth" : 264.8 * mm, "offsetDistance" : 25 * mm});
        }
        {
            var Q0;
            Q0=makeQuery(id+"F40.opExtrude","SWEPT_FACE",FACE,{"disambiguationData":[OSD([sQuery(id+"F39.wireOp",EDGE,"E52.right")])]});
            var sketch = newSketch(context, id + "F41", { "sketchPlane" : qUnion([Q0])});
            skLineSegment(sketch, "E53", {"start": v(962.28, 289.8) * mm, "end": v(1036.17, 25) * mm});
            skLineSegment(sketch, "E54", {"start": v(1036.17, 25) * mm, "end": v(1036.17, 289.8) * mm});
            skLineSegment(sketch, "E55", {"start": v(1036.17, 289.8) * mm, "end": v(962.28, 289.8) * mm});
            skSolve(sketch);
        }
        {
            var Q0;
            Q0=makeQuery(id+"F41.imprint","IMPRINT",FACE,{"disambiguationData":[TD([[makeQuery(id+"F41.imprint","IMPRINT",EDGE,{"derivedFrom":sQuery(id+"F41.wireOp",EDGE,"E53")}),1.0]])]});
            extrude(context, id + "F42", {"entities" : qUnion([Q0]), "operationType" : NewBodyOperationType.REMOVE, "oppositeDirection" : true, "depth" : 25 * mm, "offsetDistance" : 25 * mm});
        }
        {
            var Q0;
            Q0=makeQuery(id+"F26.boolean.opBoolean","MERGE",FACE,{"derivedFrom":[makeQuery(id+"F22.boolean.opBoolean","MERGE",FACE,{"derivedFrom":[makeQuery(id+"F20.opExtrude","SWEPT_FACE",FACE,{"disambiguationData":[OSD([sQuery(id+"F19.wireOp",EDGE,"E20.bottom")])]}),makeQuery(id+"F22.opExtrude","SWEPT_FACE",FACE,{"disambiguationData":[OSD([sQuery(id+"F21.wireOp",EDGE,"E21.bottom")])]}),makeQuery(id+"F22.opExtrude","SWEPT_FACE",FACE,{"disambiguationData":[OSD([sQuery(id+"F21.wireOp",EDGE,"E23.bottom")])]})]}),makeQuery(id+"F26.opExtrude","SWEPT_FACE",FACE,{"disambiguationData":[OSD([sQuery(id+"F25.wireOp",EDGE,"E40.bottom")])]}),makeQuery(id+"F26.opExtrude","SWEPT_FACE",FACE,{"disambiguationData":[OSD([sQuery(id+"F25.wireOp",EDGE,"E42.bottom")])]})]});
            var sketch = newSketch(context, id + "F43", { "sketchPlane" : qUnion([Q0])});
            skLineSegment(sketch, "E56.bottom", {"start": v(941.63, 749.17) * mm, "end": v(2081.63, 749.17) * mm});
            skLineSegment(sketch, "E56.top", {"start": v(941.63, 0) * mm, "end": v(2081.63, 0) * mm});
            skLineSegment(sketch, "E56.left", {"start": v(941.63, 749.17) * mm, "end": v(941.63, 0) * mm});
            skLineSegment(sketch, "E56.right", {"start": v(2081.63, 749.17) * mm, "end": v(2081.63, 0) * mm});
            skSolve(sketch);
        }
        {
            var Q0;
            Q0=makeQuery(id+"F43.imprint","IMPRINT",FACE,{"disambiguationData":[TD([[makeQuery(id+"F43.imprint","IMPRINT",EDGE,{"derivedFrom":sQuery(id+"F43.wireOp",EDGE,"E56.bottom")}),-1.0]])]});
            extrude(context, id + "F44", {"entities" : qUnion([Q0]), "operationType" : NewBodyOperationType.REMOVE, "oppositeDirection" : true, "depth" : 600 * mm, "offsetDistance" : 25 * mm});
        }
    });
